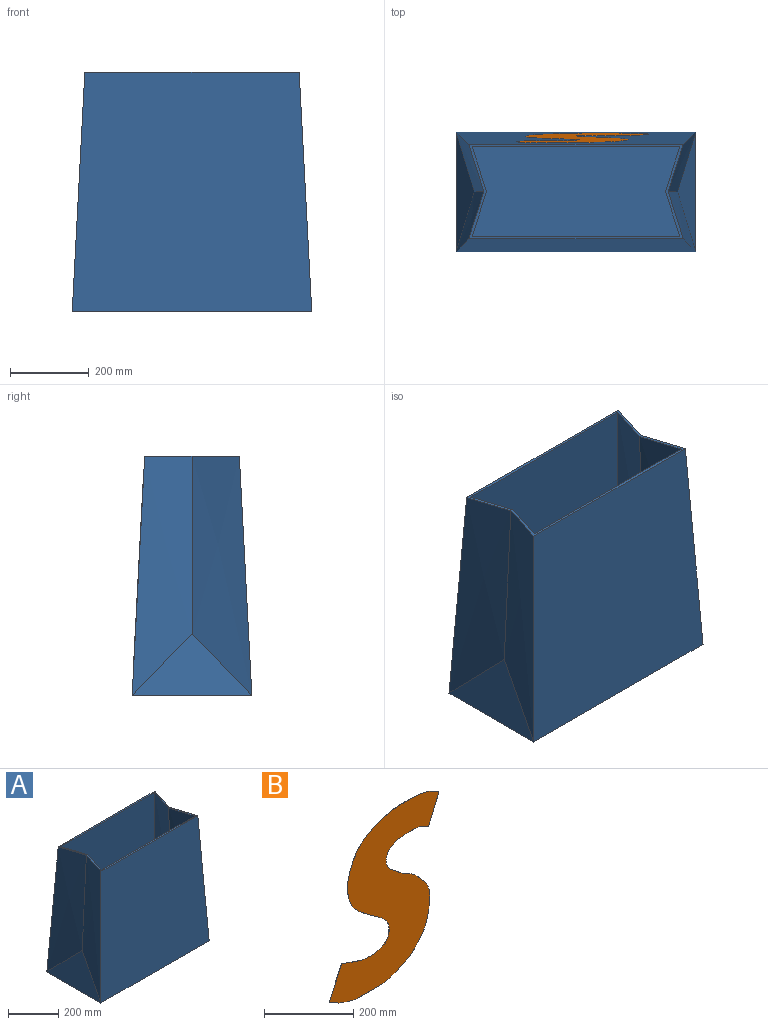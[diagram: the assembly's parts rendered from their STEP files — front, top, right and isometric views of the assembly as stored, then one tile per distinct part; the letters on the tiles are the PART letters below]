
ASSEMBLY  parts=2 mates=1
PART A: 19 faces, bbox 622.3x317.5x628.4 mm
  f0: plane 545.71x240.91mm, normal (0,0,1), area 9958.6mm2, adj f1,f2,f4,f5,f6,f8,f10,f11
  f1: bspline ~615.7x155.72mm, area 74243.3mm2, adj f0,f4,f8,f9
  f2: bspline ~615.7x155.72mm, area 74243.3mm2, adj f0,f5,f6,f7
  f3: plane 609.6x304.8mm, normal (0,0,-1), area 185806.1mm2, adj f4,f5,f7,f9
  f4: plane 609.6x609.6mm, normal (0,1,0.05), area 352620mm2, adj f0,f1,f3,f6
  f5: plane 609.6x609.6mm, normal (0,-1,0.05), area 352620mm2, adj f0,f2,f3,f8
  f6: bspline ~615.7x155.72mm, area 74243.3mm2, adj f0,f2,f4,f7
  f7: plane 304.8x158.27mm, normal (-0.96,0,0.28), area 24666.9mm2, adj f2,f3,f6
  f8: bspline ~615.7x155.72mm, area 74243.3mm2, adj f0,f1,f5,f9
  f9: plane 304.8x158.27mm, normal (0.96,0,0.28), area 24666.9mm2, adj f1,f3,f8
  f10: offset ~628.4x168.42mm, area 70268.6mm2, adj f0,f12,f13,f17,f18
  f11: offset ~628.4x168.42mm, area 70268.6mm2, adj f0,f12,f14,f15,f16
  f12: plane 592.65x291.42mm, normal (0,0,1), area 172703.9mm2, adj f10,f11,f13,f14,f15,f16,f17,f18
  f13: plane 603.25x592.65mm, normal (0,-1,-0.05), area 338601.7mm2, adj f0,f10,f12,f15
  f14: plane 603.25x592.65mm, normal (0,1,-0.05), area 338601.7mm2, adj f0,f11,f12,f17
  f15: offset ~628.4x168.42mm, area 70268.6mm2, adj f0,f11,f12,f13,f16
  f16: plane 291.4x151.78mm, normal (0.96,0,-0.28), area 22625.8mm2, adj f11,f12,f15
  f17: offset ~628.4x168.42mm, area 70268.6mm2, adj f0,f10,f12,f14,f18
  f18: plane 291.4x151.78mm, normal (-0.96,0,-0.28), area 22625.8mm2, adj f10,f12,f17
PART B: 6 faces, bbox 347.8x0.5x465.9 mm
  f0: plane 78.66x33.12mm, normal (0.92,0,-0.39), area 43.4mm2, adj f1,f3,f4,f5
  f1: extruded ~369.19x308.44mm, area 397.5mm2, adj f0,f2,f4,f5
  f2: plane 86.94x39.33mm, normal (-0.91,0,0.41), area 48.5mm2, adj f1,f3,f4,f5
  f3: extruded ~376.19x318.22mm, area 408.1mm2, adj f0,f2,f4,f5
  f4: plane 465.88x347.77mm, normal (0,-1,0), area 84938.6mm2, adj f0,f1,f2,f3
  f5: plane 465.88x347.77mm, normal (0,1,0), area 84938.6mm2, adj f0,f1,f2,f3
PLACE A t=(0,0.3,0.02)mm
PLACE B rot(axis=(0,0.03,-1),180deg) t=(14.72,135.95,319.62)mm
MATE planar B.f5 <-> A.f4  axis (0,-1,-0.05) through (7.69,136.96,300.37)mm
